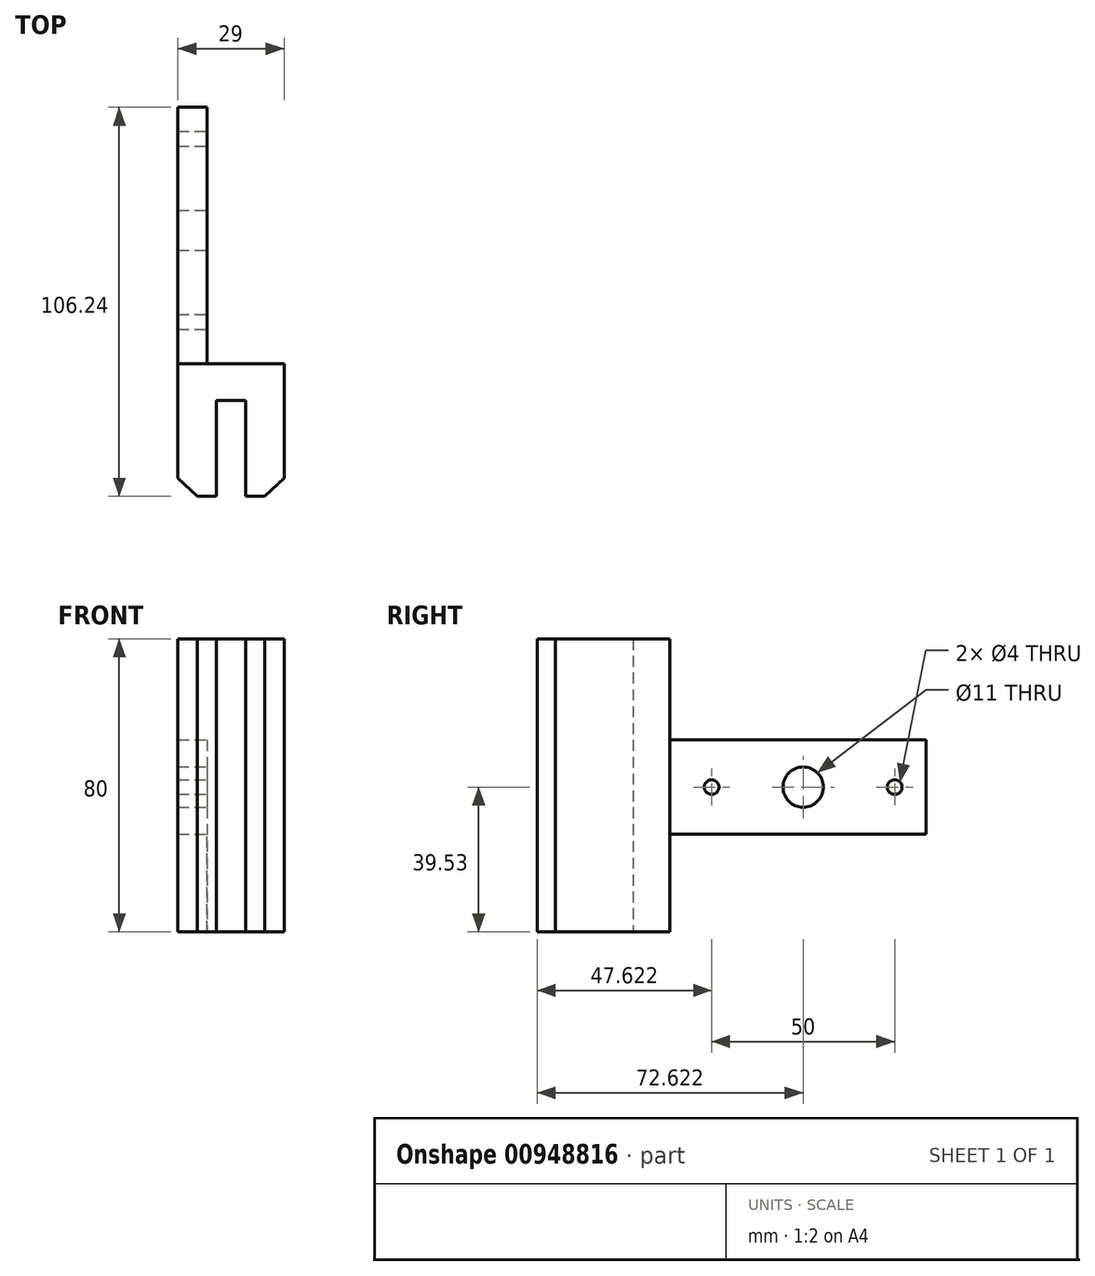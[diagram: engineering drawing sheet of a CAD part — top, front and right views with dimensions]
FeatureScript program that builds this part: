
annotation { "Feature Type Name" : "Feature", "Feature Type Description" : "" }
export const myFeature = defineFeature(function(context is Context, id is Id, definition is map)
    precondition{}
    {
        {
            var Q0;
            Q0=qCreatedBy(makeId("Top.planeOp"),FACE);
            var sketch = newSketch(context, id + "F0", { "sketchPlane" : qUnion([Q0])});
            skPoint(sketch, "E0.middle", {"position": v(0, 0) * mm});
            skLineSegment(sketch, "E1.left", {"start": v(-14.5, 18.13) * mm, "end": v(-14.5, -13.13) * mm});
            skLineSegment(sketch, "E1.right", {"start": v(14.5, 18.13) * mm, "end": v(14.5, -13.13) * mm});
            skLineSegment(sketch, "E2.left", {"start": v(-4, 8.05) * mm, "end": v(-4, -18.09) * mm});
            skLineSegment(sketch, "E2.right", {"start": v(4, 8.05) * mm, "end": v(4, -18.09) * mm});
            skPoint(sketch, "E2.middle", {"position": v(0, -3.09) * mm});
            skLineSegment(sketch, "E3", {"start": v(-9.25, -18.1) * mm, "end": v(-4, -18.09) * mm});
            skLineSegment(sketch, "E4", {"start": v(4, -18.09) * mm, "end": v(9.25, -18.1) * mm});
            skLineSegment(sketch, "E5", {"start": v(-9.25, -18.1) * mm, "end": v(-14.5, -13.13) * mm});
            skLineSegment(sketch, "E6", {"start": v(9.25, -18.1) * mm, "end": v(14.5, -13.13) * mm});
            skPoint(sketch, "E7.orphan", {"position": v(-14.5, -18.13) * mm});
            skPoint(sketch, "E8.orphan", {"position": v(14.5, -18.13) * mm});
            skLineSegment(sketch, "E9.top", {"start": v(-14.5, 88.13) * mm, "end": v(-6.5, 88.13) * mm});
            skLineSegment(sketch, "E9.left", {"start": v(-14.5, 18.13) * mm, "end": v(-14.5, 88.13) * mm});
            skLineSegment(sketch, "E9.right", {"start": v(-6.5, 18.13) * mm, "end": v(-6.5, 88.13) * mm});
            skLineSegment(sketch, "E10", {"start": v(-6.5, 18.13) * mm, "end": v(14.5, 18.13) * mm});
            skLineSegment(sketch, "E11", {"start": v(-4, 8.05) * mm, "end": v(4, 8.05) * mm});
            skPoint(sketch, "E12.orphan", {"position": v(-4, 11.91) * mm});
            skPoint(sketch, "E13.orphan", {"position": v(4, 11.91) * mm});
            skSolve(sketch);
        }
        {
            var Q0;
            Q0=makeQuery(id+"F0.imprint","IMPRINT",FACE,{"disambiguationData":[TD([[makeQuery(id+"F0.imprint","IMPRINT",EDGE,{"derivedFrom":sQuery(id+"F0.wireOp",EDGE,"E1.left")}),1.0]])]});
            extrude(context, id + "F1", {"entities" : qUnion([Q0]), "depth" : 80 * mm, "offsetDistance" : 25 * mm});
        }
        {
            var Q0;
            Q0=qCreatedBy(makeId("Right.planeOp"),FACE);
            var sketch = newSketch(context, id + "F2", { "sketchPlane" : qUnion([Q0])});
            skLineSegment(sketch, "E14.top", {"start": v(88.13, 26.66) * mm, "end": v(23.51, 26.66) * mm});
            skLineSegment(sketch, "E14.left", {"start": v(88.13, 52.4) * mm, "end": v(88.13, 26.66) * mm});
            skLineSegment(sketch, "E14.right", {"start": v(23.51, 52.4) * mm, "end": v(23.51, 26.66) * mm});
            skLineSegment(sketch, "E15.bottom", {"start": v(88.13, 39.53) * mm, "end": v(23.51, 39.53) * mm, "construction": true});
            skLineSegment(sketch, "E15.top", {"start": v(88.13, 39.53) * mm, "end": v(23.51, 39.53) * mm, "construction": true});
            skLineSegment(sketch, "E15.left", {"start": v(88.13, 39.53) * mm, "end": v(88.13, 39.53) * mm});
            skLineSegment(sketch, "E15.right", {"start": v(23.51, 39.53) * mm, "end": v(23.51, 39.53) * mm});
            skLineSegment(sketch, "E16.bottom", {"start": v(88.13, 52.4) * mm, "end": v(18.13, 52.4) * mm});
            skLineSegment(sketch, "E16.top", {"start": v(88.13, 80) * mm, "end": v(18.13, 80) * mm});
            skLineSegment(sketch, "E16.left", {"start": v(88.13, 52.4) * mm, "end": v(88.13, 80) * mm});
            skCircle(sketch, "E17", {"center": v(29.51, 39.53) * mm, "radius": 2 * mm});
            skCircle(sketch, "E18", {"center": v(54.51, 39.53) * mm, "radius": 5.5 * mm});
            skCircle(sketch, "E19", {"center": v(79.51, 39.53) * mm, "radius": 2 * mm});
            skLineSegment(sketch, "E20.MirrorCS", {"start": v(88.13, 26.66) * mm, "end": v(88.13, -0.94) * mm});
            skLineSegment(sketch, "E21.bottom", {"start": v(23.51, 26.66) * mm, "end": v(19, 26.66) * mm});
            skLineSegment(sketch, "E21.top", {"start": v(23.51, 0) * mm, "end": v(18.15, 0) * mm});
            skPoint(sketch, "E22.orphan", {"position": v(93.6, 79.06) * mm});
            skPoint(sketch, "E23.MirrorCS.end.orphan", {"position": v(23.51, 52.4) * mm});
            skPoint(sketch, "E23.MirrorCS.start.orphan", {"position": v(23.51, 79.06) * mm});
            skPoint(sketch, "E24.orphan", {"position": v(93.6, 0) * mm});
            skLineSegment(sketch, "E25.bottom", {"start": v(88.13, 26.66) * mm, "end": v(18.15, 26.66) * mm});
            skLineSegment(sketch, "E25.top", {"start": v(88.13, -0.94) * mm, "end": v(18.15, -0.94) * mm});
            skLineSegment(sketch, "E25.right", {"start": v(18.15, 26.66) * mm, "end": v(18.15, -0.94) * mm});
            skPoint(sketch, "E26", {"position": v(23.38, 92.77) * mm});
            skPoint(sketch, "E27", {"position": v(22.26, 88.58) * mm});
            skLineSegment(sketch, "E28.bottom", {"start": v(89.93, 80) * mm, "end": v(18.13, 80) * mm});
            skLineSegment(sketch, "E28.top", {"start": v(89.93, 52.4) * mm, "end": v(18.13, 52.4) * mm});
            skLineSegment(sketch, "E28.left", {"start": v(89.93, 80) * mm, "end": v(89.93, 52.4) * mm});
            skLineSegment(sketch, "E28.right", {"start": v(18.13, 80) * mm, "end": v(18.13, 52.4) * mm});
            skPoint(sketch, "E29.right.start.orphan", {"position": v(23.51, 0) * mm});
            skSolve(sketch);
        }
        {
            var Q0;
            {var subQ3=sQuery(id+"F2.wireOp",EDGE,"E16.left");Q0=makeQuery(id+"F2.imprint","IMPRINT",FACE,{"disambiguationData":[TD([[makeQuery(id+"F2.imprint","IMPRINT",EDGE,{"derivedFrom":subQ3}),1.0]])]});}
            var Q1;
            {var subQ1=sQuery(id+"F2.wireOp",EDGE,"E25.top");Q1=makeQuery(id+"F2.imprint","IMPRINT",FACE,{"disambiguationData":[TD([[makeQuery(id+"F2.imprint","IMPRINT",EDGE,{"derivedFrom":subQ1}),-1.0]])]});}
            var Q2;
            Q2=makeQuery(id+"F2.imprint","IMPRINT",FACE,{"disambiguationData":[TD([[makeQuery(id+"F2.imprint","IMPRINT",EDGE,{"derivedFrom":sQuery(id+"F2.wireOp",EDGE,"E19")}),1.0]])]});
            var Q3;
            Q3=makeQuery(id+"F2.imprint","IMPRINT",FACE,{"disambiguationData":[TD([[makeQuery(id+"F2.imprint","IMPRINT",EDGE,{"derivedFrom":sQuery(id+"F2.wireOp",EDGE,"E18")}),1.0]])]});
            var Q4;
            Q4=makeQuery(id+"F2.imprint","IMPRINT",FACE,{"disambiguationData":[TD([[makeQuery(id+"F2.imprint","IMPRINT",EDGE,{"derivedFrom":sQuery(id+"F2.wireOp",EDGE,"E17")}),1.0]])]});
            extrude(context, id + "F3", {"entities" : qUnion([Q0, Q1, Q2, Q3, Q4]), "operationType" : NewBodyOperationType.REMOVE, "oppositeDirection" : true, "depth" : 25 * mm, "offsetDistance" : 25 * mm});
        }
    });
